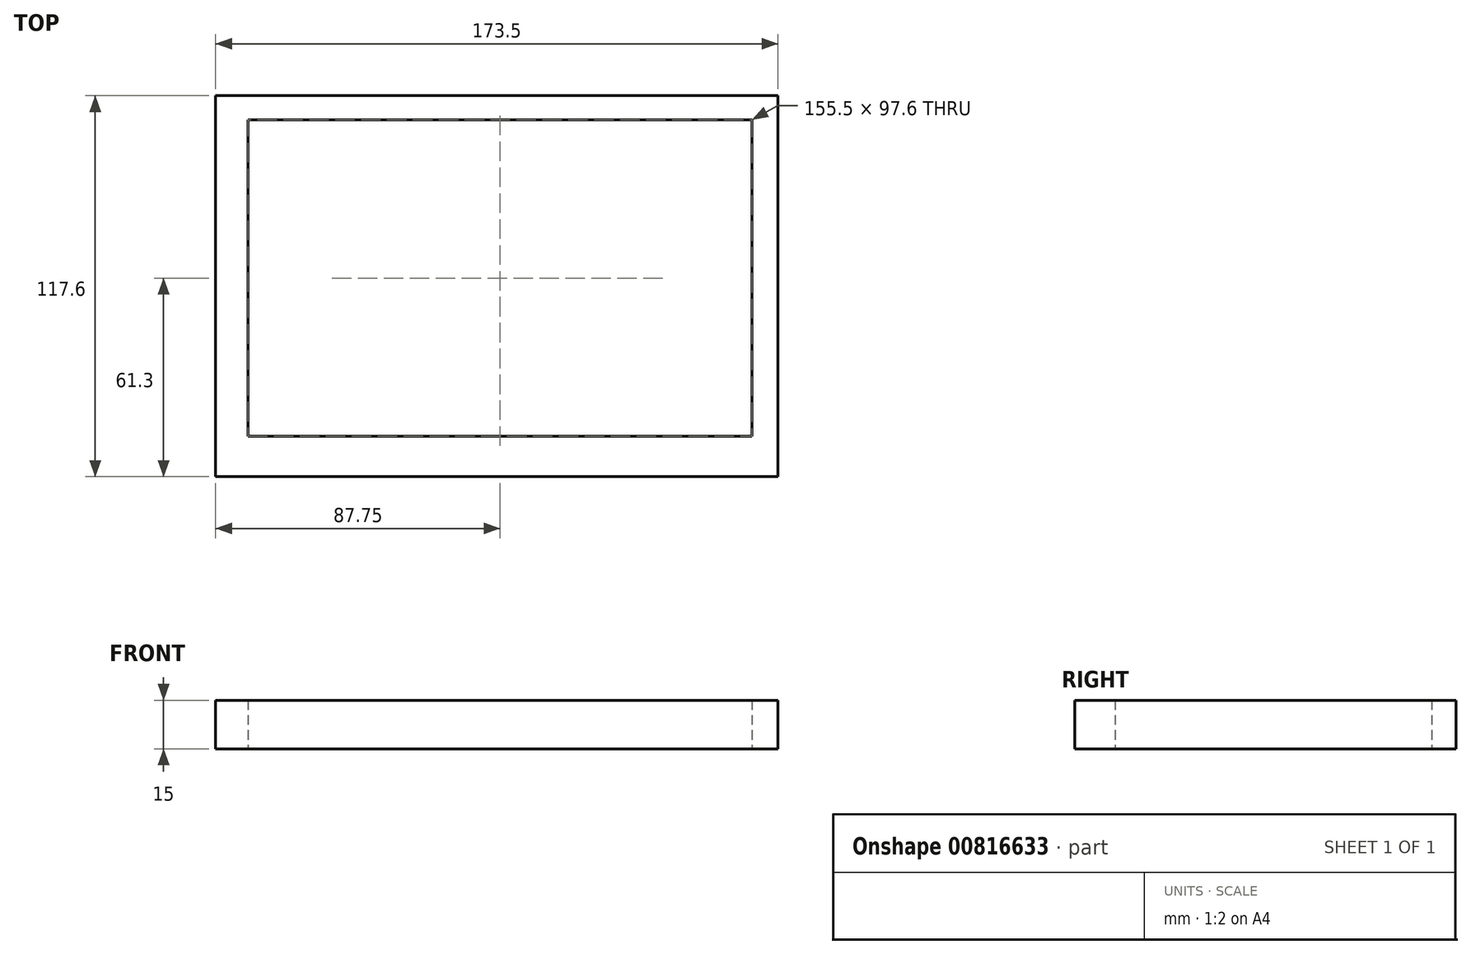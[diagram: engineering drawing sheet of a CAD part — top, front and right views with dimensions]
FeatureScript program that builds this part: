
annotation { "Feature Type Name" : "Feature", "Feature Type Description" : "" }
export const myFeature = defineFeature(function(context is Context, id is Id, definition is map)
    precondition{}
    {
        {
            var Q0;
            Q0=qCreatedBy(makeId("Top.planeOp"),FACE);
            var sketch = newSketch(context, id + "F0", { "sketchPlane" : qUnion([Q0])});
            skLineSegment(sketch, "E0.bottom", {"start": v(-81.75, 53.8) * mm, "end": v(81.75, 53.8) * mm});
            skLineSegment(sketch, "E0.top", {"start": v(-81.75, -53.8) * mm, "end": v(81.75, -53.8) * mm});
            skLineSegment(sketch, "E0.left", {"start": v(-81.75, 53.8) * mm, "end": v(-81.75, -53.8) * mm});
            skLineSegment(sketch, "E0.right", {"start": v(81.75, 53.8) * mm, "end": v(81.75, -53.8) * mm});
            skPoint(sketch, "E0.middle", {"position": v(0, 0) * mm});
            skSolve(sketch);
        }
        {
            var Q0;
            Q0=qCreatedBy(makeId("Top.planeOp"),FACE);
            var sketch = newSketch(context, id + "F1", { "sketchPlane" : qUnion([Q0])});
            skLineSegment(sketch, "E1.bottom", {"start": v(-80.75, 52.8) * mm, "end": v(80.75, 52.8) * mm});
            skLineSegment(sketch, "E1.top", {"start": v(-80.75, -52.8) * mm, "end": v(80.75, -52.8) * mm});
            skLineSegment(sketch, "E1.left", {"start": v(-80.75, 52.8) * mm, "end": v(-80.75, -52.8) * mm});
            skLineSegment(sketch, "E1.right", {"start": v(80.75, 52.8) * mm, "end": v(80.75, -52.8) * mm});
            skPoint(sketch, "E1.middle", {"position": v(0, 0) * mm});
            skSolve(sketch);
        }
        {
            var Q0;
            Q0=makeQuery(id+"F0.imprint","IMPRINT",FACE,{"disambiguationData":[TD([[makeQuery(id+"F0.imprint","IMPRINT",EDGE,{"derivedFrom":sQuery(id+"F0.wireOp",EDGE,"E0.bottom")}),-1.0]])]});
            var sketch = newSketch(context, id + "F2", { "sketchPlane" : qUnion([Q0])});
            skLineSegment(sketch, "E2.bottom", {"start": v(-76.75, 51.3) * mm, "end": v(78.75, 51.3) * mm});
            skLineSegment(sketch, "E2.top", {"start": v(-76.75, -46.3) * mm, "end": v(78.75, -46.3) * mm});
            skLineSegment(sketch, "E2.left", {"start": v(-76.75, 51.3) * mm, "end": v(-76.75, -46.3) * mm});
            skLineSegment(sketch, "E2.right", {"start": v(78.75, 51.3) * mm, "end": v(78.75, -46.3) * mm});
            skSolve(sketch);
        }
        {
            var Q0;
            Q0=makeQuery(id+"F0.imprint","IMPRINT",FACE,{"disambiguationData":[TD([[makeQuery(id+"F0.imprint","IMPRINT",EDGE,{"derivedFrom":sQuery(id+"F0.wireOp",EDGE,"E0.bottom")}),-1.0]])]});
            var sketch = newSketch(context, id + "F3", { "sketchPlane" : qUnion([Q0])});
            skLineSegment(sketch, "E3.bottom", {"start": v(-86.75, 58.8) * mm, "end": v(86.75, 58.8) * mm});
            skLineSegment(sketch, "E3.top", {"start": v(-86.75, -58.8) * mm, "end": v(86.75, -58.8) * mm});
            skLineSegment(sketch, "E3.left", {"start": v(-86.75, 58.8) * mm, "end": v(-86.75, -58.8) * mm});
            skLineSegment(sketch, "E3.right", {"start": v(86.75, 58.8) * mm, "end": v(86.75, -58.8) * mm});
            skSolve(sketch);
        }
        {
            var Q0;
            Q0 = qSketchRegion(id + "F3", true);
            extrude(context, id + "F4", {"entities" : qUnion([Q0]), "depth" : 15 * mm, "offsetDistance" : 25 * mm});
        }
        {
            var Q0;
            Q0=makeQuery(id+"F2.imprint","IMPRINT",FACE,{"disambiguationData":[TD([[makeQuery(id+"F2.imprint","IMPRINT",EDGE,{"derivedFrom":sQuery(id+"F2.wireOp",EDGE,"E2.bottom")}),-1.0]])]});
            extrude(context, id + "F5", {"entities" : qUnion([Q0]), "operationType" : NewBodyOperationType.REMOVE, "depth" : 15 * mm, "offsetDistance" : 25 * mm});
        }
        {
            var Q0;
            Q0 = qSketchRegion(id + "F1", true);
            extrude(context, id + "F6", {"entities" : qUnion([Q0]), "operationType" : NewBodyOperationType.REMOVE, "oppositeDirection" : true, "depth" : 13 * mm, "offsetDistance" : 25 * mm});
        }
    });
